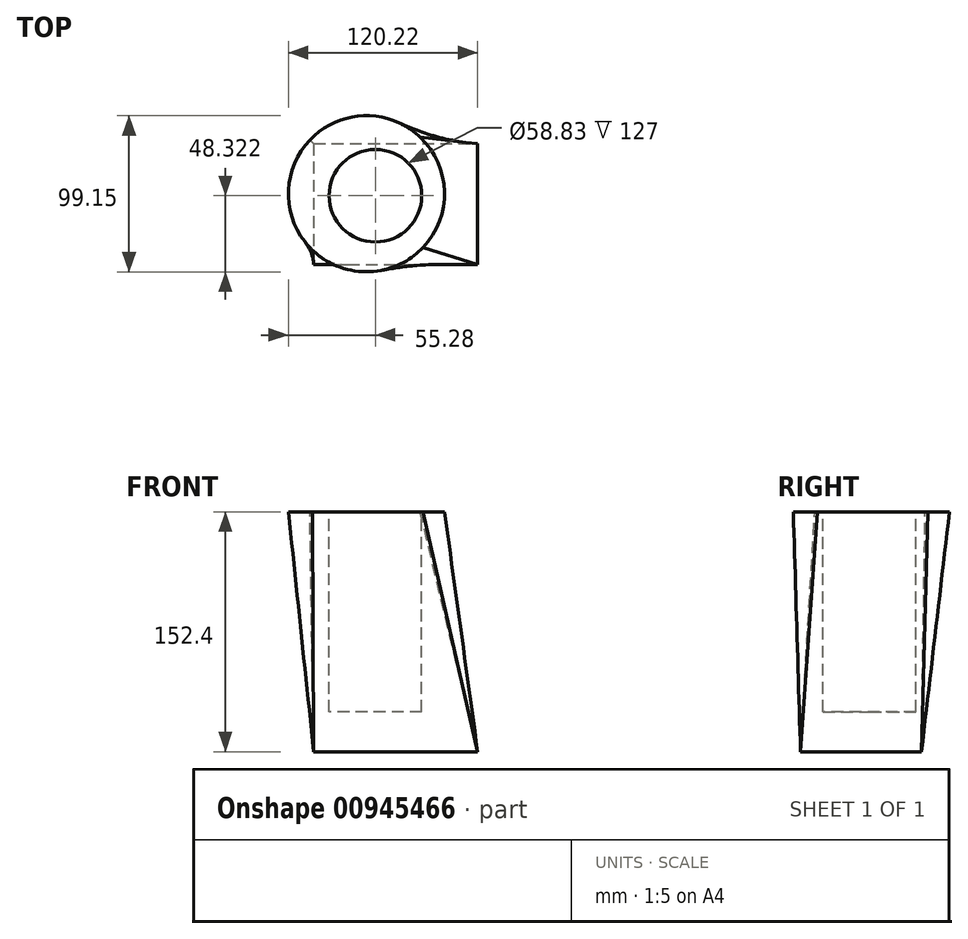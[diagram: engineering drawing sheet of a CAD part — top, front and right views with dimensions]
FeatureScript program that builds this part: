
annotation { "Feature Type Name" : "Feature", "Feature Type Description" : "" }
export const myFeature = defineFeature(function(context is Context, id is Id, definition is map)
    precondition{}
    {
        {
            var Q0;
            Q0=qCreatedBy(makeId("Top.planeOp"),FACE);
            var sketch = newSketch(context, id + "F0", { "sketchPlane" : qUnion([Q0])});
            skLineSegment(sketch, "E0.bottom", {"start": v(-39.21, 38.4) * mm, "end": v(64.94, 38.4) * mm});
            skLineSegment(sketch, "E0.top", {"start": v(-39.21, -38.4) * mm, "end": v(64.94, -38.4) * mm});
            skLineSegment(sketch, "E0.left", {"start": v(-39.21, 38.4) * mm, "end": v(-39.21, -38.4) * mm});
            skLineSegment(sketch, "E0.right", {"start": v(64.94, 38.4) * mm, "end": v(64.94, -38.4) * mm});
            skPoint(sketch, "E0.middle", {"position": v(12.87, 0) * mm});
            skSolve(sketch);
        }
        {
            var Q0;
            Q0=qCreatedBy(makeId("Top.planeOp"),FACE);
            cPlane(context, id + "F1", {"entities" : qUnion([Q0]), "cplaneType" : CPlaneType.OFFSET, "offset" : 152.4 * mm, "width" : 152.4 * mm, "height" : 152.4 * mm});
        }
        {
            var Q0;
            Q0=qCreatedBy(id+"F1.planeOp",FACE);
            var sketch = newSketch(context, id + "F2", { "sketchPlane" : qUnion([Q0])});
            skCircle(sketch, "E1", {"center": v(-5.7, 6.58) * mm, "radius": 49.57 * mm});
            skSolve(sketch);
        }
        {
            var Q0;
            Q0=makeQuery(id+"F0.imprint","IMPRINT",FACE,{"disambiguationData":[TD([[makeQuery(id+"F0.imprint","IMPRINT",EDGE,{"derivedFrom":sQuery(id+"F0.wireOp",EDGE,"E0.bottom")}),-1.0]])]});
            var Q1;
            Q1=makeQuery(id+"F2.imprint","IMPRINT",FACE,{"disambiguationData":[TD([[makeQuery(id+"F2.imprint","IMPRINT",EDGE,{"derivedFrom":sQuery(id+"F2.wireOp",EDGE,"E1")}),1.0]])]});
            loft(context, id + "F3", {"sheetProfilesArray" : [{ "sheetProfileEntities" : qUnion([Q0]) }, { "sheetProfileEntities" : qUnion([Q1]) }]});
        }
        {
            var Q0;
            Q0=makeQuery(id+"F3.opLoft","CAP_FACE",FACE,{"disambiguationData":[OSD([makeQuery(id+"F2.imprint","IMPRINT",FACE,{"disambiguationData":[TD([[makeQuery(id+"F2.imprint","IMPRINT",EDGE,{"derivedFrom":sQuery(id+"F2.wireOp",EDGE,"E1")}),1.0]])]})])],"isStart":true});
            var sketch = newSketch(context, id + "F4", { "sketchPlane" : qUnion([Q0])});
            skCircle(sketch, "E2", {"center": v(0, 5.32) * mm, "radius": 29.41 * mm});
            skSolve(sketch);
        }
        {
            var Q0;
            Q0 = qSketchRegion(id + "F4", true);
            extrude(context, id + "F5", {"entities" : qUnion([Q0]), "operationType" : NewBodyOperationType.REMOVE, "oppositeDirection" : true, "depth" : 127 * mm, "offsetDistance" : 25.4 * mm});
        }
    });
